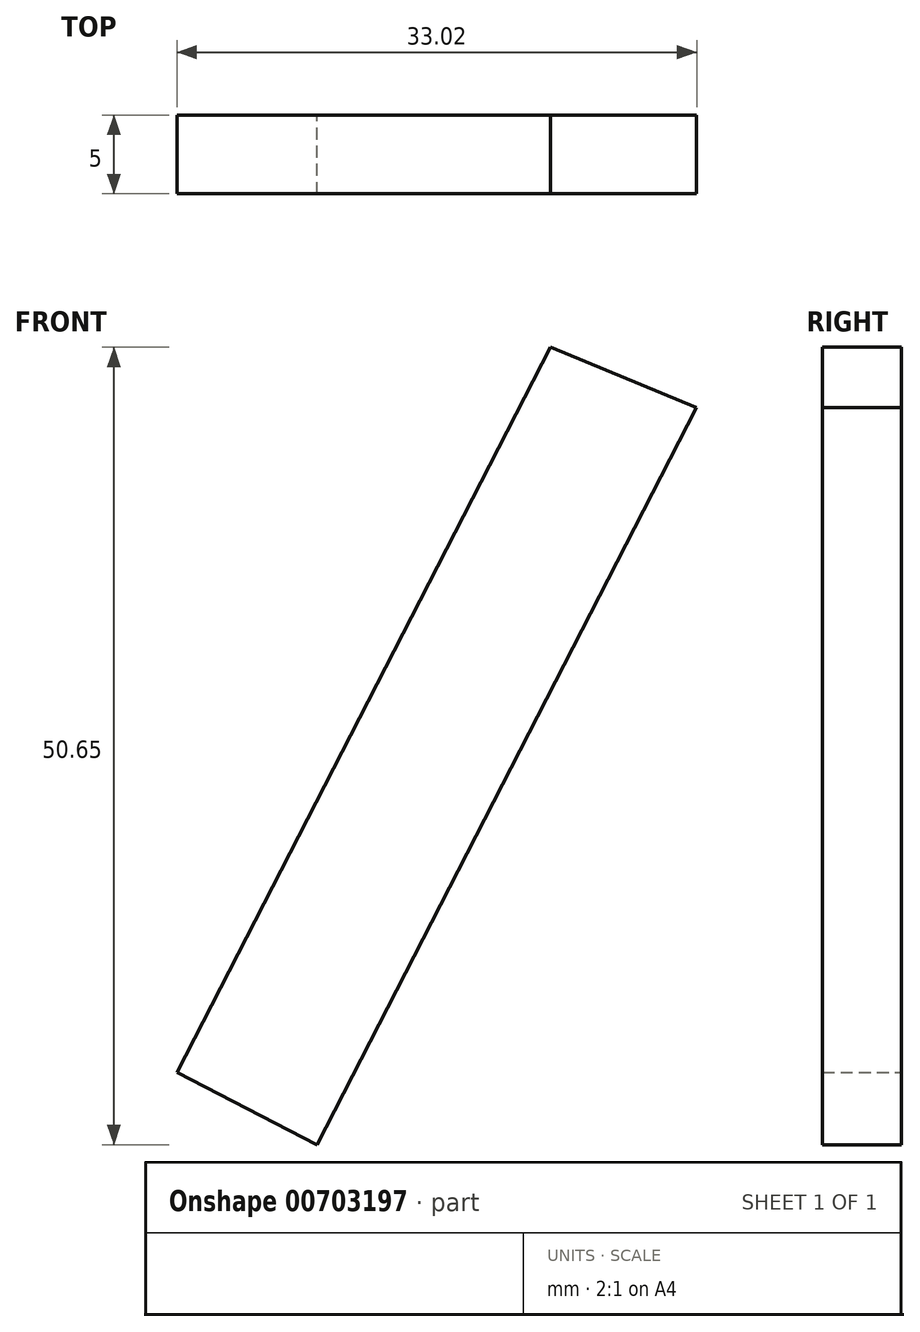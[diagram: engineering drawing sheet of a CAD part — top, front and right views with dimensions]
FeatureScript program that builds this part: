
annotation { "Feature Type Name" : "Feature", "Feature Type Description" : "" }
export const myFeature = defineFeature(function(context is Context, id is Id, definition is map)
    precondition{}
    {
        {
            var Q0;
            Q0=qCreatedBy(makeId("Front.planeOp"),FACE);
            var sketch = newSketch(context, id + "F0", { "sketchPlane" : qUnion([Q0])});
            skLineSegment(sketch, "E0", {"start": v(-16.66, 46.82) * mm, "end": v(-40.79, 0) * mm});
            skLineSegment(sketch, "E1", {"start": v(-40.79, 0) * mm, "end": v(-49.68, 4.58) * mm});
            skLineSegment(sketch, "E2", {"start": v(-49.68, 4.58) * mm, "end": v(-25.94, 50.65) * mm});
            skLineSegment(sketch, "E3", {"start": v(-25.94, 50.65) * mm, "end": v(-16.66, 46.82) * mm});
            skSolve(sketch);
        }
        {
            var Q0;
            Q0=makeQuery(id+"F0.imprint","IMPRINT",FACE,{"disambiguationData":[TD([[makeQuery(id+"F0.imprint","IMPRINT",EDGE,{"derivedFrom":sQuery(id+"F0.wireOp",EDGE,"E0")}),-1.0]])]});
            extrude(context, id + "F1", {"entities" : qUnion([Q0]), "depth" : 5 * mm, "offsetDistance" : 25 * mm});
        }
    });
